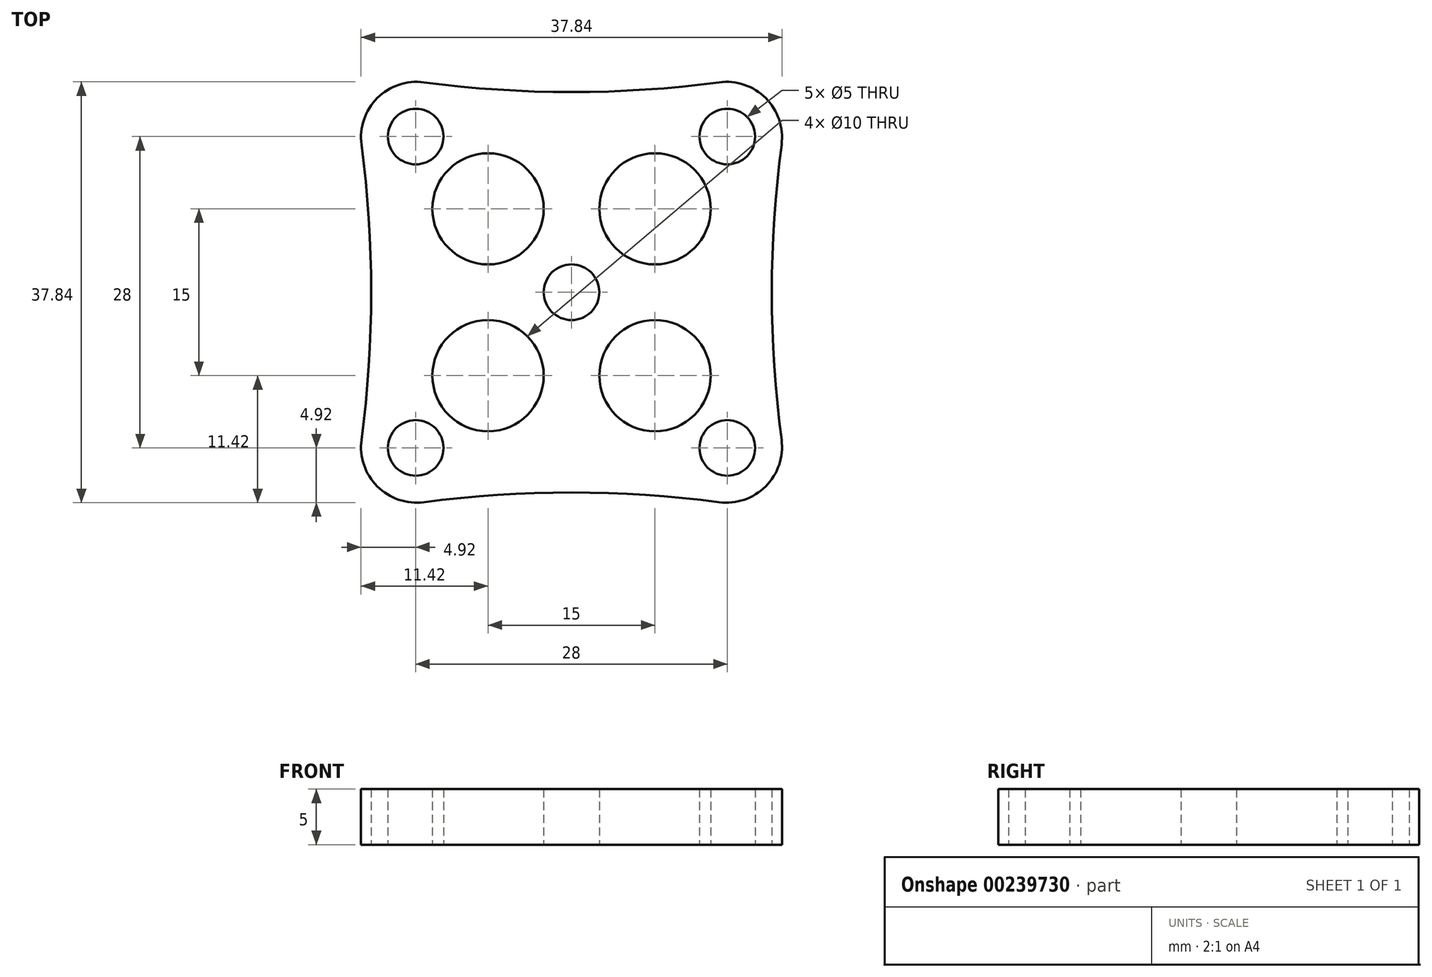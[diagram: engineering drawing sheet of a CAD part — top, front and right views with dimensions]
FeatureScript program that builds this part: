
annotation { "Feature Type Name" : "Feature", "Feature Type Description" : "" }
export const myFeature = defineFeature(function(context is Context, id is Id, definition is map)
    precondition{}
    {
        {
            var Q0;
            Q0=qCreatedBy(makeId("Top.planeOp"),FACE);
            var sketch = newSketch(context, id + "F0", { "sketchPlane" : qUnion([Q0])});
            skLineSegment(sketch, "E0.bottom", {"start": v(7.5, -7.5) * mm, "end": v(-7.5, -7.5) * mm});
            skLineSegment(sketch, "E0.top", {"start": v(7.5, 7.5) * mm, "end": v(-7.5, 7.5) * mm});
            skLineSegment(sketch, "E0.left", {"start": v(7.5, -7.5) * mm, "end": v(7.5, 7.5) * mm});
            skLineSegment(sketch, "E0.right", {"start": v(-7.5, -7.5) * mm, "end": v(-7.5, 7.5) * mm});
            skPoint(sketch, "E0.middle", {"position": v(0, 0) * mm});
            skCircle(sketch, "E1", {"center": v(-7.5, 7.5) * mm, "radius": 5 * mm});
            skCircle(sketch, "E2", {"center": v(7.5, 7.5) * mm, "radius": 5 * mm});
            skCircle(sketch, "E3", {"center": v(-7.5, -7.5) * mm, "radius": 5 * mm});
            skCircle(sketch, "E4", {"center": v(7.5, -7.5) * mm, "radius": 5 * mm});
            skCircle(sketch, "E5", {"center": v(-7.5, 7.5) * mm, "radius": 2 * mm});
            skCircle(sketch, "E6", {"center": v(7.5, 7.5) * mm, "radius": 2 * mm});
            skCircle(sketch, "E7", {"center": v(7.5, -7.5) * mm, "radius": 2 * mm});
            skCircle(sketch, "E8", {"center": v(-7.5, -7.5) * mm, "radius": 2 * mm});
            skCircle(sketch, "E9", {"center": v(0, 0) * mm, "radius": 2.5 * mm});
            skLineSegment(sketch, "E10.bottom", {"start": v(20, -20) * mm, "end": v(-20, -20) * mm});
            skLineSegment(sketch, "E10.top", {"start": v(20, 20) * mm, "end": v(-20, 20) * mm});
            skLineSegment(sketch, "E10.left", {"start": v(20, -20) * mm, "end": v(20, 20) * mm});
            skLineSegment(sketch, "E10.right", {"start": v(-20, -20) * mm, "end": v(-20, 20) * mm});
            skPoint(sketch, "E11.centerSnap0", {"position": v(0, -20) * mm});
            skCircle(sketch, "E12.cCircle", {"center": v(0, 0) * mm, "radius": 14 * mm, "construction": true});
            skLineSegment(sketch, "E12.0", {"start": v(14, 14) * mm, "end": v(14, -14) * mm});
            skLineSegment(sketch, "E12.1", {"start": v(14, -14) * mm, "end": v(-14, -14) * mm});
            skLineSegment(sketch, "E12.2", {"start": v(-14, -14) * mm, "end": v(-14, 14) * mm});
            skLineSegment(sketch, "E12.3", {"start": v(-14, 14) * mm, "end": v(14, 14) * mm});
            skPoint(sketch, "E12.0.midPoint", {"position": v(14, 0) * mm});
            skCircle(sketch, "E13", {"center": v(14, 14) * mm, "radius": 2.5 * mm});
            skCircle(sketch, "E14", {"center": v(-14, -14) * mm, "radius": 2.5 * mm});
            skCircle(sketch, "E15", {"center": v(14, -14) * mm, "radius": 2.5 * mm});
            skCircle(sketch, "E16", {"center": v(-14, 14) * mm, "radius": 2.5 * mm});
            skArc(sketch, "E17", {"start": v(-20, 20) * mm, "mid": v(0, 18) * mm, "end": v(20, 20) * mm});
            skArc(sketch, "E18", {"start": v(20, 20) * mm, "mid": v(18, 0) * mm, "end": v(20, -20) * mm});
            skArc(sketch, "E19", {"start": v(20, -20) * mm, "mid": v(0, -18) * mm, "end": v(-20, -20) * mm});
            skArc(sketch, "E20", {"start": v(-20, -20) * mm, "mid": v(-18, 0) * mm, "end": v(-20, 20) * mm});
            skSolve(sketch);
        }
        {
            var Q0;
            Q0=makeQuery(id+"F0.imprint","IMPRINT",FACE,{"disambiguationData":[TD([[makeQuery(id+"F0.imprint","IMPRINT",EDGE,{"derivedFrom":sQuery(id+"F0.wireOp",EDGE,"E17")}),-1.0]])]});
            var Q1;
            {var subQ5=sQuery(id+"F0.wireOp",EDGE,"E4");var subQ6=sQuery(id+"F0.wireOp",EDGE,"E0.bottom");var subQ7=makeQuery(id+"F0.imprint","INTERSECT",VERTEX,{"derivedFrom":[subQ6,subQ5]});Q1=makeQuery(id+"F0.imprint","IMPRINT",FACE,{"disambiguationData":[TD([[makeQuery(id+"F0.imprint","IMPRINT",EDGE,{"disambiguationData":[TD([[subQ7,-1.0]])],"derivedFrom":subQ6}),1.0]])]});}
            var Q2;
            Q2=makeQuery(id+"F0.imprint","IMPRINT",FACE,{"disambiguationData":[TD([[makeQuery(id+"F0.imprint","IMPRINT",EDGE,{"derivedFrom":sQuery(id+"F0.wireOp",EDGE,"E9")}),-1.0]])]});
            extrude(context, id + "F1", {"entities" : qUnion([Q0, Q1, Q2]), "depth" : 5 * mm});
        }
        {
            var Q0;
            Q0=makeQuery(id+"F1.opExtrude","SWEPT_EDGE",EDGE,{"disambiguationData":[OSD([sQuery(id+"F0.wireOp",EDGE,"E10.bottom"),sQuery(id+"F0.wireOp",EDGE,"E10.left"),sQuery(id+"F0.wireOp",EDGE,"E18"),sQuery(id+"F0.wireOp",EDGE,"E19")])]});
            var Q1;
            Q1=makeQuery(id+"F1.opExtrude","SWEPT_EDGE",EDGE,{"disambiguationData":[OSD([sQuery(id+"F0.wireOp",EDGE,"E10.bottom"),sQuery(id+"F0.wireOp",EDGE,"E10.right"),sQuery(id+"F0.wireOp",EDGE,"E19"),sQuery(id+"F0.wireOp",EDGE,"E20")])]});
            var Q2;
            Q2=makeQuery(id+"F1.opExtrude","SWEPT_EDGE",EDGE,{"disambiguationData":[OSD([sQuery(id+"F0.wireOp",EDGE,"E10.top"),sQuery(id+"F0.wireOp",EDGE,"E10.left"),sQuery(id+"F0.wireOp",EDGE,"E17"),sQuery(id+"F0.wireOp",EDGE,"E18")])]});
            var Q3;
            Q3=makeQuery(id+"F1.opExtrude","SWEPT_EDGE",EDGE,{"disambiguationData":[OSD([sQuery(id+"F0.wireOp",EDGE,"E10.top"),sQuery(id+"F0.wireOp",EDGE,"E10.right"),sQuery(id+"F0.wireOp",EDGE,"E17"),sQuery(id+"F0.wireOp",EDGE,"E20")])]});
            fillet(context, id + "F2", {"entities" : qUnion([Q0, Q1, Q2, Q3]), "radius" : 5 * mm, "tangentPropagation" : true, "allowEdgeOverflow" : false});
        }
    });
